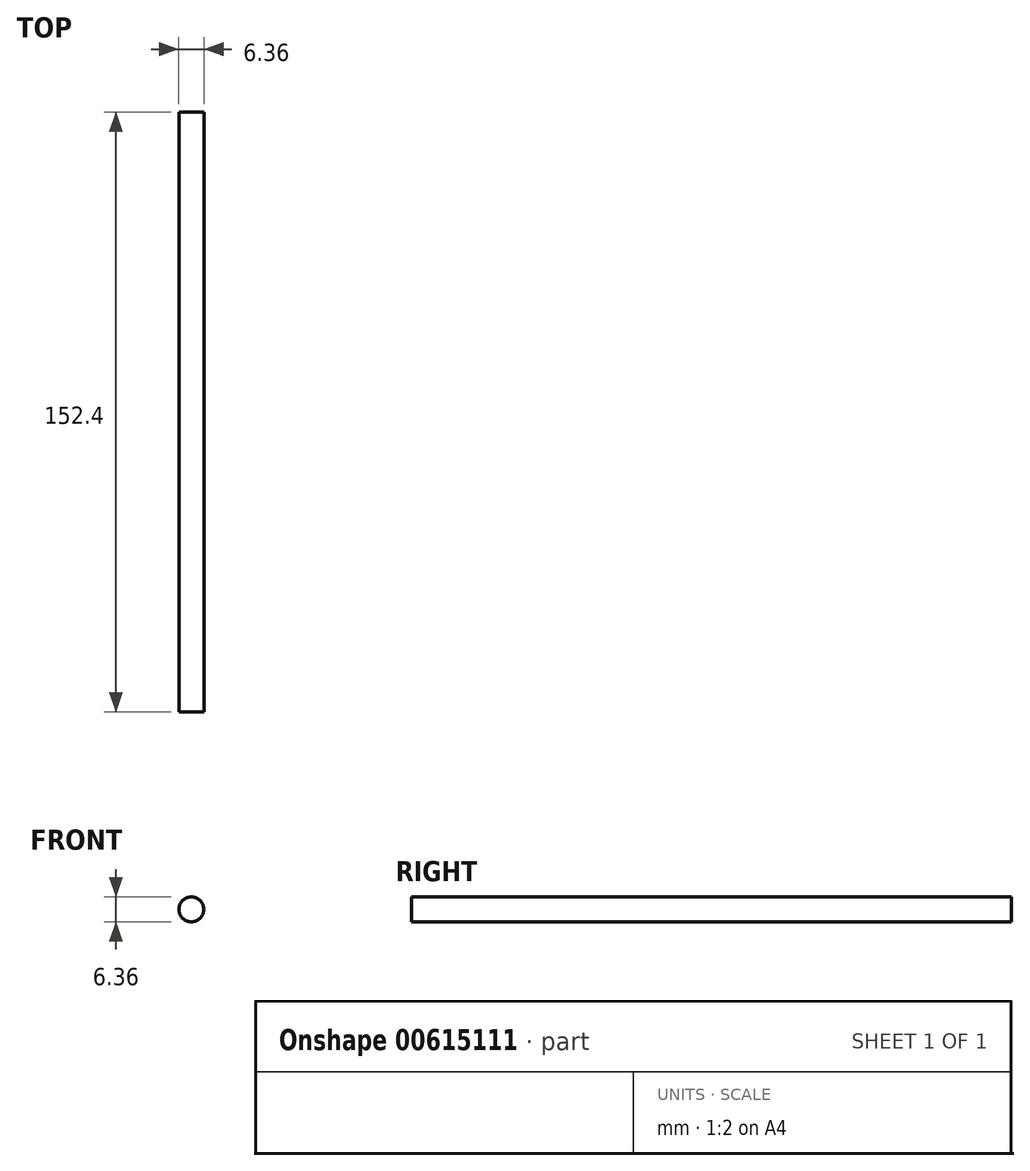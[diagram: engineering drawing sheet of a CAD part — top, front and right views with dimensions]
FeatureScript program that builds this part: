
annotation { "Feature Type Name" : "Feature", "Feature Type Description" : "" }
export const myFeature = defineFeature(function(context is Context, id is Id, definition is map)
    precondition{}
    {
        {
            var Q0;
            Q0=qCreatedBy(makeId("Front.planeOp"),FACE);
            var sketch = newSketch(context, id + "F0", { "sketchPlane" : qUnion([Q0])});
            skCircle(sketch, "E0", {"center": v(0, 0) * mm, "radius": 3.18 * mm});
            skSolve(sketch);
        }
        {
            var Q0;
            Q0 = qSketchRegion(id + "F0", true);
            extrude(context, id + "F1", {"entities" : qUnion([Q0]), "endBound" : BoundingType.SYMMETRIC, "depth" : 152.4 * mm, "offsetDistance" : 25.4 * mm});
        }
    });
